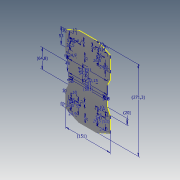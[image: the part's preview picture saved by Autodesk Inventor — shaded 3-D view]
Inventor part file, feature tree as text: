
AUTODESK INVENTOR PART (.ipt)
format: ipt  version: 2013 (Build 170138000, 138)  size: 183,296 bytes
history: native  units: mm
features: sketch x3, extrude x1
ambient origin geometry x8: Origin, YZ Plane, XZ Plane, XY Plane, X Axis, Y Axis, Z Axis, Center Point
bodies: Solid1 (feature_tree)
feature tree (4):
  extrude  "Extrusion1"  Depth=10.0mm
  sketch  "Sketch2"  dims[d27=10.0mm]
  sketch  "Sketch3"  dims[d28=10.0mm d29=53.0mm d30=10.0mm d31=24.9mm d32=53.0mm d33=10.0mm d35=24.9mm d36=10.0mm d37=53.0mm d38=24.9mm d39=53.0mm d40=10.0mm d41=53.0mm d42=24.9mm d43=53.0mm d44=10.0mm d45=53.0mm d47=131.0mm d48=10.0mm d49=131.0mm d50=54.8mm d51=48.0mm d52=131.0mm d53=2.0mm d54=131.0mm d68=5.0mm d70=5.0mm d71=5.0mm d73=5.0mm d74=5.0mm d76=23.0mm d77=32.15mm d78=32.15mm d86=5.0mm d88=5.0mm d90=5.0mm d92=41.4mm d93=5.0mm d94=41.4mm d98=41.4mm d99=5.0mm d100=41.4mm d101=5.0mm d104=26.5mm d105=5.0mm d106=26.5mm d107=5.0mm d108=26.5mm d109=5.0mm d110=26.5mm d111=5.0mm d116=271.3mm d117=151.0mm d118=64.8mm d119=20.0mm]
  sketch  "Sketch1"  dims[d24=2.0mm d25=0.0mm d26=10.0mm]
